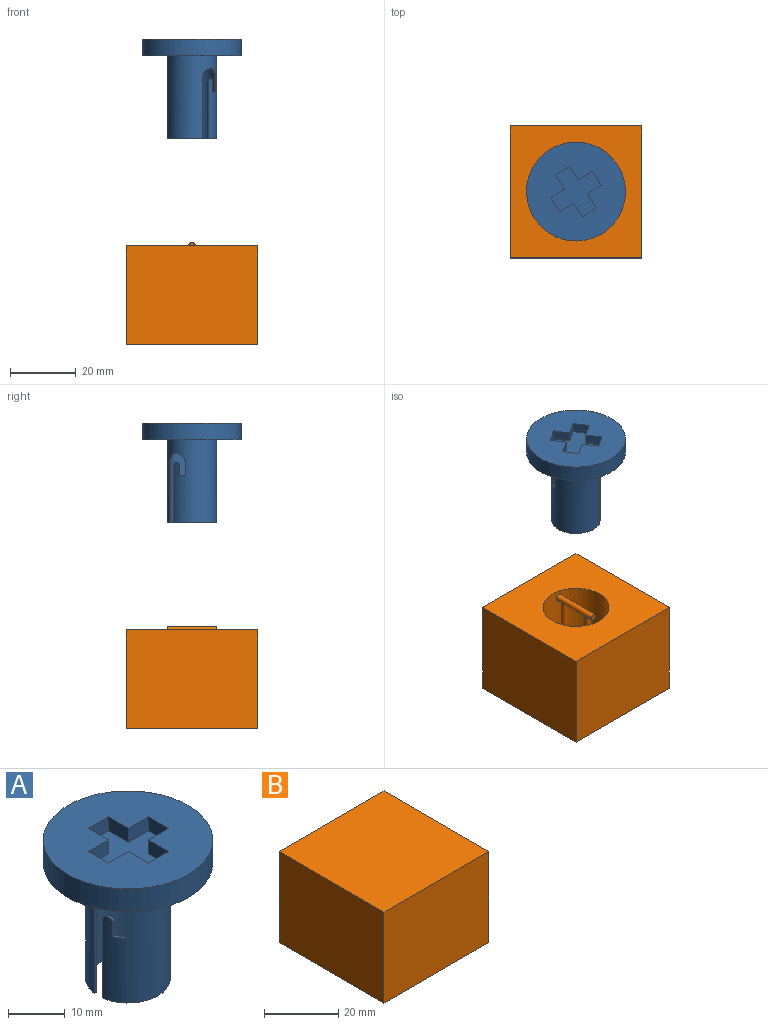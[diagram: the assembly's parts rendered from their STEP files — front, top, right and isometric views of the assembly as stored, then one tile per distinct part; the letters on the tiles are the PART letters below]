
ASSEMBLY  parts=2 mates=1
PART A: 35 faces, bbox 30x30x30 mm
  f0: plane 30x30mm, normal (0,0,1), area 581.9mm2, adj f7,f22,f23,f24,f25,f26,f27,f28
  f1: plane 14.87x6.5mm, normal (0,0,-1), area 10.4mm2, adj f2,f4,f9,f16
  f2: cylinder r=7mm len=25mm, axis (0,0,1), area 976.1mm2, adj f1,f3,f5,f8,f9,f10,f11,f12
  f3: plane 14.87x6.5mm, normal (0,0,-1), area 10.4mm2, adj f2,f4,f8,f15
  f4: cylinder r=7.5mm len=25mm, axis (0,0,1), area 1055.7mm2, adj f1,f3,f6,f8,f9,f10,f11,f12
  f5: plane 14x14mm, normal (0,0,-1), area 153.9mm2, adj f2
  f6: plane 30x30mm, normal (0,0,-1), area 530.1mm2, adj f4,f7
  f7: cylinder r=15mm len=30mm, axis (0,0,1), area 471.2mm2, adj f0,f6
  f8: plane 17x0.51mm, normal (0,1,0), area 8.6mm2, adj f2,f3,f4,f14
  f9: plane 18x0.51mm, normal (0,-1,0), area 9.1mm2, adj f1,f2,f4,f10
  f10: cylinder r=3mm len=6mm, axis (1,0,0), area 5.2mm2, adj f2,f4,f9,f11
  f11: plane 4x0.69mm, normal (0,1,0), area 2.8mm2, adj f2,f4,f10,f12
  f12: plane 2x1.98mm, normal (0,0,1), area 1.2mm2, adj f2,f4,f11,f13
  f13: plane 3x0.55mm, normal (0,-1,0), area 1.6mm2, adj f2,f4,f12,f14
  f14: cylinder r=1mm len=2mm, axis (1,0,0), area 1.6mm2, adj f2,f4,f8,f13
  f15: plane 18x0.51mm, normal (0,1,0), area 9.1mm2, adj f2,f3,f4,f21
  f16: plane 17x0.51mm, normal (0,-1,0), area 8.6mm2, adj f1,f2,f4,f17
  f17: cylinder r=1mm len=2mm, axis (-1,0,0), area 1.6mm2, adj f2,f4,f16,f18
  f18: plane 3x0.55mm, normal (0,1,0), area 1.6mm2, adj f2,f4,f17,f19
  f19: plane 2x1.98mm, normal (0,0,1), area 1.2mm2, adj f2,f4,f18,f20
  f20: plane 4x0.69mm, normal (0,-1,0), area 2.8mm2, adj f2,f4,f19,f21
  f21: cylinder r=3mm len=6mm, axis (-1,0,0), area 5.2mm2, adj f2,f4,f15,f20
  f22: plane 5x3mm, normal (-1,0,0), area 15mm2, adj f0,f23,f33,f34
  f23: plane 5x3mm, normal (0,1,0), area 15mm2, adj f0,f22,f24,f34
  f24: plane 5x3mm, normal (-1,0,0), area 15mm2, adj f0,f23,f25,f34
  f25: plane 5x3mm, normal (0,-1,0), area 15mm2, adj f0,f24,f26,f34
  f26: plane 5x3mm, normal (-1,0,0), area 15mm2, adj f0,f25,f27,f34
  f27: plane 5x3mm, normal (0,-1,0), area 15mm2, adj f0,f26,f28,f34
  f28: plane 5x3mm, normal (1,0,0), area 15mm2, adj f0,f27,f29,f34
  f29: plane 5x3mm, normal (0,-1,0), area 15mm2, adj f0,f28,f30,f34
  f30: plane 5x3mm, normal (1,0,0), area 15mm2, adj f0,f29,f31,f34
  f31: plane 5x3mm, normal (0,1,0), area 15mm2, adj f0,f30,f32,f34
  f32: plane 5x3mm, normal (1,0,0), area 15mm2, adj f0,f31,f33,f34
  f33: plane 5x3mm, normal (0,1,0), area 15mm2, adj f0,f22,f32,f34
  f34: plane 15x15mm, normal (0,0,1), area 125mm2, adj f22,f23,f24,f25,f26,f27,f28,f29
PART B: 13 faces, bbox 40x40x31 mm
  f0: plane 20x20mm, normal (0,0,-1), area 307.9mm2, adj f1,f2,f6
  f1: cylinder r=1mm len=28mm, axis (0,0,-1), area 171.9mm2, adj f0,f3
  f2: cylinder r=1mm len=28mm, axis (0,0,-1), area 171.9mm2, adj f0,f3
  f3: cylinder r=1mm len=15mm, axis (0,1,0), area 86.2mm2, adj f1,f2,f4,f5
  f4: plane 2x2mm, normal (0,-1,0), area 3.1mm2, adj f3
  f5: plane 2x2mm, normal (0,1,0), area 3.1mm2, adj f3
  f6: cylinder r=10mm len=28mm, axis (0,0,1), area 1759.3mm2, adj f0,f7
  f7: plane 40x40mm, normal (0,0,-1), area 1285.8mm2, adj f6,f9,f10,f11,f12
  f8: plane 40x40mm, normal (0,0,1), area 1600mm2, adj f9,f10,f11,f12
  f9: plane 40x30mm, normal (0,1,0), area 1200mm2, adj f7,f8,f10,f12
  f10: plane 40x30mm, normal (1,0,0), area 1200mm2, adj f7,f8,f9,f11
  f11: plane 40x30mm, normal (0,-1,0), area 1200mm2, adj f7,f8,f10,f12
  f12: plane 40x30mm, normal (-1,0,0), area 1200mm2, adj f7,f8,f9,f11
PLACE A rot(axis=(0,0,1),122.7deg) t=(0,0,82.71)mm
PLACE B rot(axis=(-1,0,0),180deg) t=(0,0,30)mm fixed
MATE cylindrical B.f6 <-> A.f2  axis (0,0,1) through (0,0,30)mm
